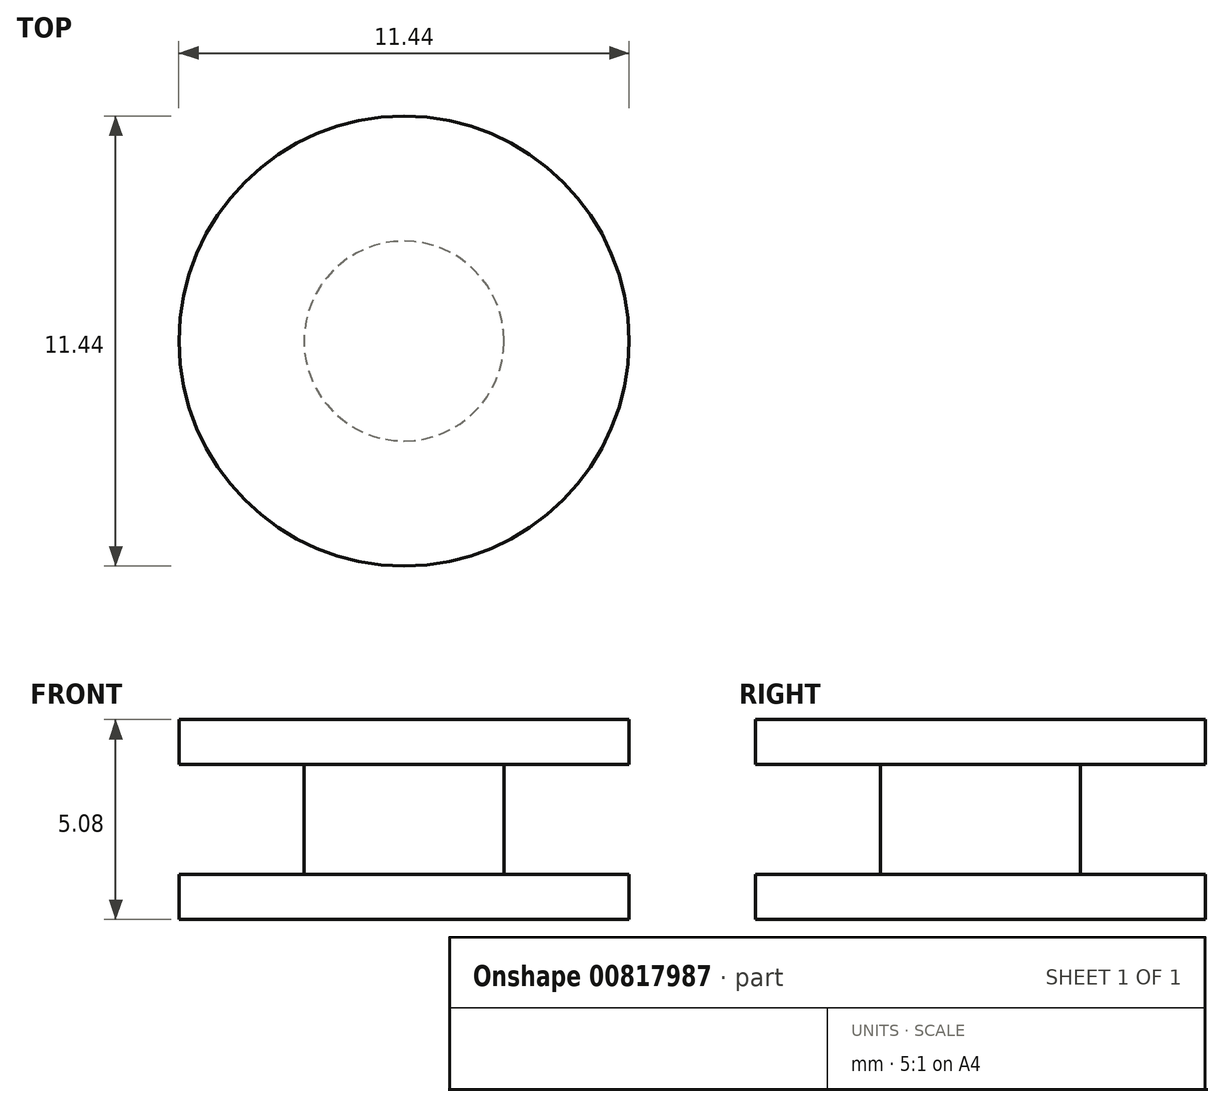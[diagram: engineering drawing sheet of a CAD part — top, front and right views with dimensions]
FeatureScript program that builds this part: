
annotation { "Feature Type Name" : "Feature", "Feature Type Description" : "" }
export const myFeature = defineFeature(function(context is Context, id is Id, definition is map)
    precondition{}
    {
        {
            var Q0;
            Q0=qCreatedBy(makeId("Top.planeOp"),FACE);
            var sketch = newSketch(context, id + "F0", { "sketchPlane" : qUnion([Q0])});
            skCircle(sketch, "E0", {"center": v(0, 0) * mm, "radius": 2.54 * mm});
            skCircle(sketch, "E1", {"center": v(0, 0) * mm, "radius": 5.72 * mm});
            skSolve(sketch);
        }
        {
            var Q0;
            Q0=makeQuery(id+"F0.imprint","IMPRINT",FACE,{"disambiguationData":[TD([[makeQuery(id+"F0.imprint","IMPRINT",EDGE,{"derivedFrom":sQuery(id+"F0.wireOp",EDGE,"E0")}),1.0]])]});
            var Q1;
            Q1=makeQuery(id+"F0.imprint","IMPRINT",FACE,{"disambiguationData":[TD([[makeQuery(id+"F0.imprint","IMPRINT",EDGE,{"derivedFrom":sQuery(id+"F0.wireOp",EDGE,"E0")}),-1.0]])]});
            extrude(context, id + "F1", {"entities" : qUnion([Q0, Q1]), "endBound" : BoundingType.SYMMETRIC, "depth" : 5.08 * mm, "offsetDistance" : 25.4 * mm});
        }
        {
            var Q0;
            Q0 = qSketchRegion(id + "F0", true);
            extrude(context, id + "F2", {"entities" : qUnion([Q0]), "operationType" : NewBodyOperationType.REMOVE, "endBound" : BoundingType.SYMMETRIC, "oppositeDirection" : true, "depth" : 2.8 * mm, "offsetDistance" : 25.4 * mm});
        }
    });
